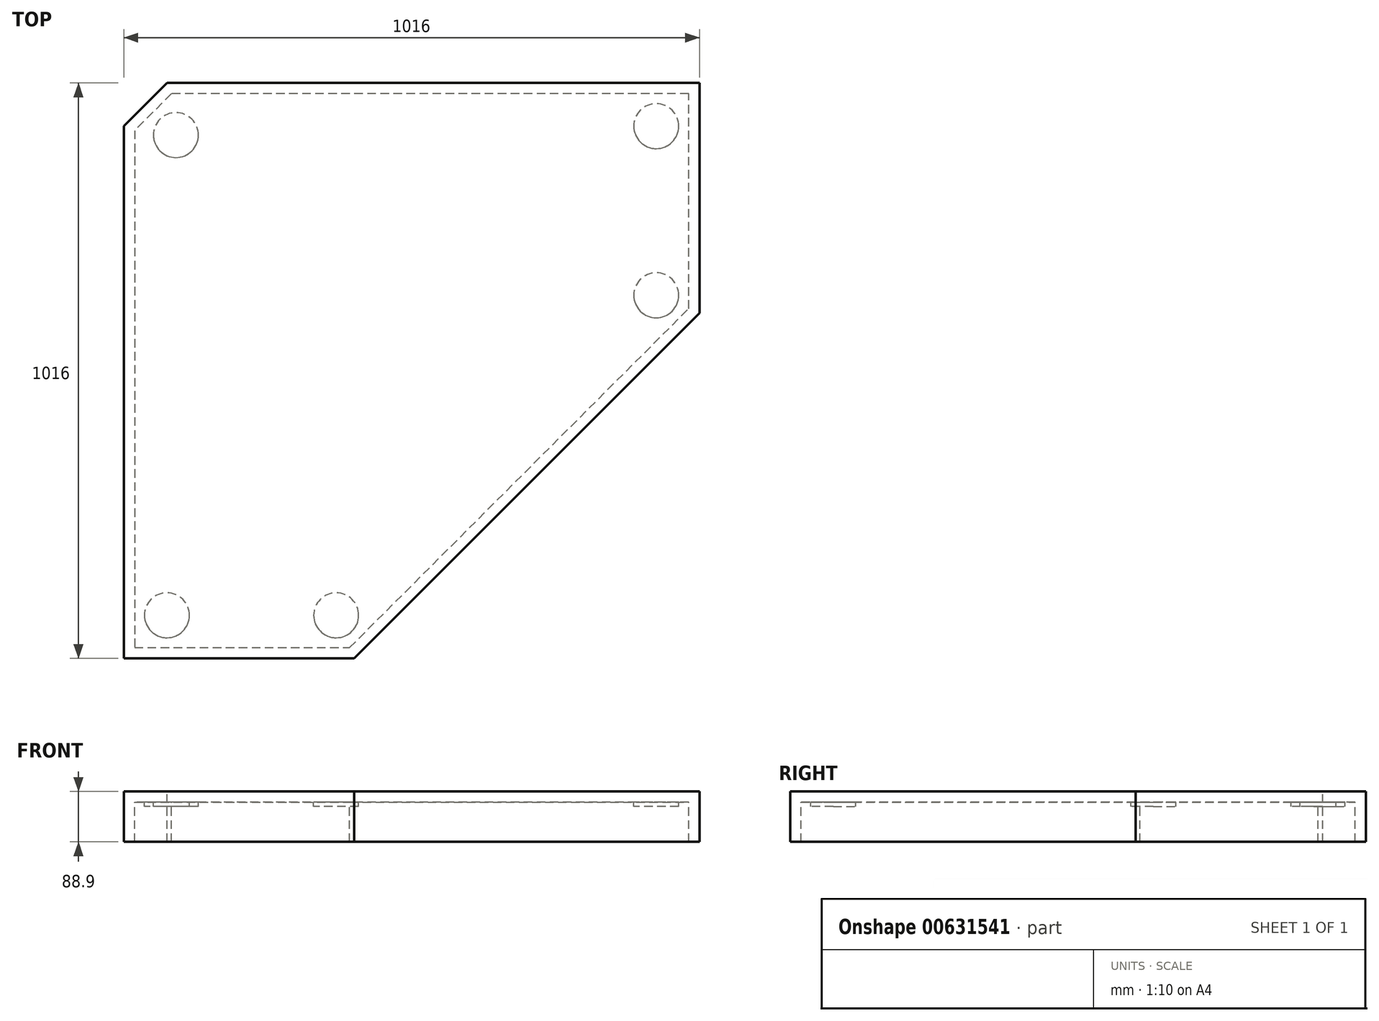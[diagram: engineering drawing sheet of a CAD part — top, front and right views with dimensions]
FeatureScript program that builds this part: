
annotation { "Feature Type Name" : "Feature", "Feature Type Description" : "" }
export const myFeature = defineFeature(function(context is Context, id is Id, definition is map)
    precondition{}
    {
        {
            var Q0;
            Q0=qCreatedBy(makeId("Top.planeOp"),FACE);
            var sketch = newSketch(context, id + "F0", { "sketchPlane" : qUnion([Q0])});
            skLineSegment(sketch, "E0", {"start": v(0, -1016) * mm, "end": v(406.4, -1016) * mm});
            skLineSegment(sketch, "E1", {"start": v(406.4, -1016) * mm, "end": v(1016, -406.4) * mm});
            skLineSegment(sketch, "E2", {"start": v(1016, -406.4) * mm, "end": v(1016, 0) * mm});
            skLineSegment(sketch, "E3", {"start": v(1016, 0) * mm, "end": v(76.2, 0) * mm});
            skLineSegment(sketch, "E4", {"start": v(76.2, 0) * mm, "end": v(0, -76.2) * mm});
            skLineSegment(sketch, "E5", {"start": v(0, -76.2) * mm, "end": v(0, -1016) * mm});
            skLineSegment(sketch, "E6.0", {"start": v(19.05, -996.95) * mm, "end": v(398.5, -996.95) * mm});
            skLineSegment(sketch, "E6.1", {"start": v(996.95, -398.5) * mm, "end": v(996.95, -19.05) * mm});
            skLineSegment(sketch, "E6.2", {"start": v(996.95, -19.05) * mm, "end": v(84.1, -19.05) * mm});
            skLineSegment(sketch, "E6.3", {"start": v(398.5, -996.95) * mm, "end": v(996.95, -398.5) * mm});
            skLineSegment(sketch, "E6.4", {"start": v(84.1, -19.05) * mm, "end": v(19.05, -84.1) * mm});
            skLineSegment(sketch, "E6.5", {"start": v(19.05, -84.1) * mm, "end": v(19.05, -996.95) * mm});
            skSolve(sketch);
        }
        {
            var Q0;
            Q0=qSketchRegion(id+"F0",true);
            extrude(context, id + "F1", {"entities" : qUnion([Q0]), "oppositeDirection" : true, "depth" : 88.9 * mm, "offsetDistance" : 25.4 * mm});
        }
        {
            var Q0;
            Q0=makeQuery(id+"F0.imprint","IMPRINT",FACE,{"disambiguationData":[TD([[makeQuery(id+"F0.imprint","IMPRINT",EDGE,{"derivedFrom":sQuery(id+"F0.wireOp",EDGE,"E6.0")}),1.0]])]});
            extrude(context, id + "F2", {"entities" : qUnion([Q0]), "operationType" : NewBodyOperationType.ADD, "oppositeDirection" : true, "depth" : 19.05 * mm, "offsetDistance" : 25.4 * mm});
        }
        {
            var Q0;
            Q0=makeQuery(id+"F2.opExtrude","CAP_FACE",FACE,{"disambiguationData":[OSD([sQuery(id+"F0.wireOp",EDGE,"E6.0"),sQuery(id+"F0.wireOp",EDGE,"E6.1"),sQuery(id+"F0.wireOp",EDGE,"E6.2"),sQuery(id+"F0.wireOp",EDGE,"E6.3"),sQuery(id+"F0.wireOp",EDGE,"E6.4"),sQuery(id+"F0.wireOp",EDGE,"E6.5")])],"isStart":false});
            var sketch = newSketch(context, id + "F3", { "sketchPlane" : qUnion([Q0])});
            skLineSegment(sketch, "E7.0", {"start": v(939.8, 76.2) * mm, "end": v(107.76, 76.2) * mm, "construction": true});
            skLineSegment(sketch, "E7.1", {"start": v(76.2, 107.76) * mm, "end": v(76.2, 939.8) * mm, "construction": true});
            skLineSegment(sketch, "E7.2", {"start": v(76.2, 939.8) * mm, "end": v(374.84, 939.8) * mm, "construction": true});
            skLineSegment(sketch, "E7.3", {"start": v(107.76, 76.2) * mm, "end": v(76.2, 107.76) * mm, "construction": true});
            skLineSegment(sketch, "E7.4", {"start": v(374.84, 939.8) * mm, "end": v(939.8, 374.84) * mm, "construction": true});
            skLineSegment(sketch, "E7.5", {"start": v(939.8, 374.84) * mm, "end": v(939.8, 76.2) * mm, "construction": true});
            skCircle(sketch, "E8", {"center": v(76.2, 939.8) * mm, "radius": 39.69 * mm});
            skCircle(sketch, "E9", {"center": v(91.98, 91.98) * mm, "radius": 39.69 * mm});
            skCircle(sketch, "E10", {"center": v(374.84, 939.8) * mm, "radius": 39.69 * mm});
            skCircle(sketch, "E11", {"center": v(939.8, 374.84) * mm, "radius": 39.69 * mm});
            skCircle(sketch, "E12", {"center": v(939.8, 76.2) * mm, "radius": 39.69 * mm});
            skSolve(sketch);
        }
        {
            var Q0;
            Q0=qSketchRegion(id+"F3",true);
            extrude(context, id + "F4", {"entities" : qUnion([Q0]), "operationType" : NewBodyOperationType.ADD, "depth" : 7.62 * mm, "offsetDistance" : 25.4 * mm});
        }
    });
